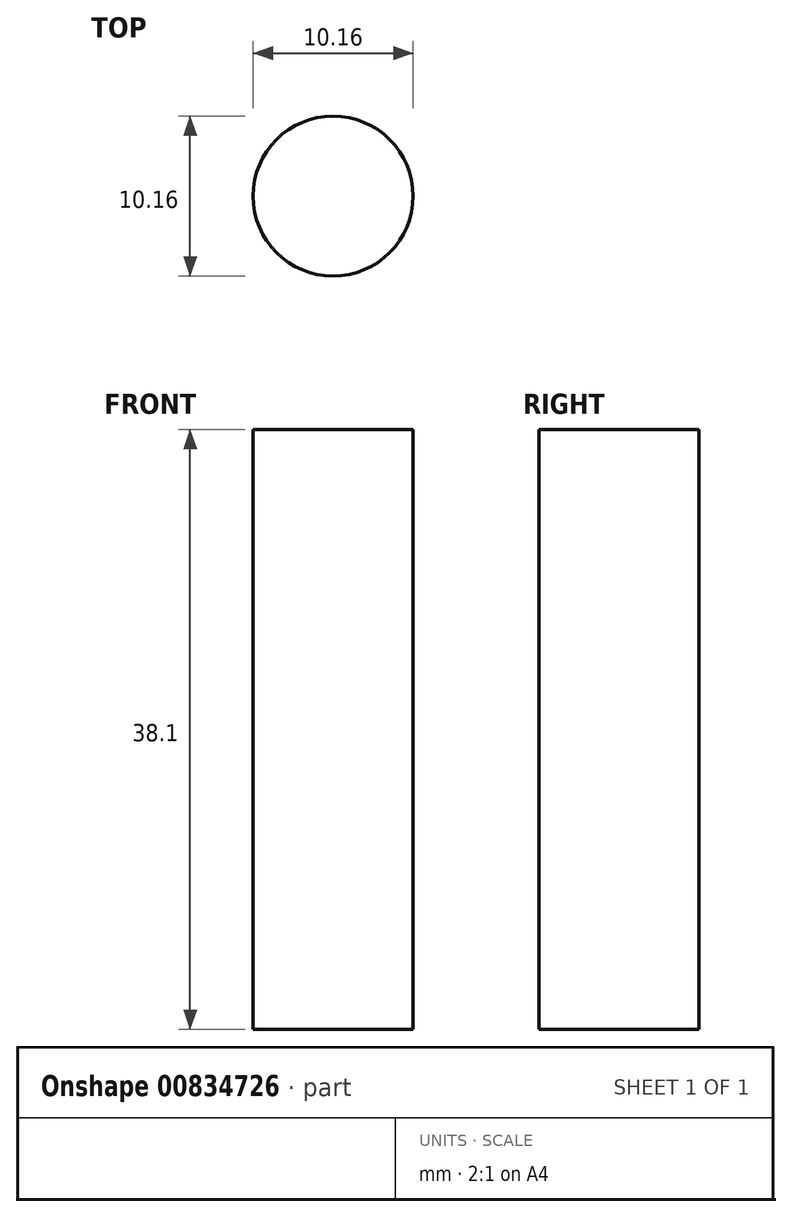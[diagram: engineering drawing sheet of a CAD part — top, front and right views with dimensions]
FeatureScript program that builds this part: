
annotation { "Feature Type Name" : "Feature", "Feature Type Description" : "" }
export const myFeature = defineFeature(function(context is Context, id is Id, definition is map)
    precondition{}
    {
        {
            var Q0;
            Q0=qCreatedBy(makeId("Front.planeOp"),FACE);
            var sketch = newSketch(context, id + "F0", { "sketchPlane" : qUnion([Q0])});
            skLineSegment(sketch, "E0.bottom", {"start": v(-5.9, 16.9) * mm, "end": v(4.26, 16.9) * mm});
            skLineSegment(sketch, "E0.top", {"start": v(-5.9, -21.2) * mm, "end": v(4.26, -21.2) * mm});
            skLineSegment(sketch, "E0.left", {"start": v(-5.9, 16.9) * mm, "end": v(-5.9, -21.2) * mm});
            skLineSegment(sketch, "E0.right", {"start": v(4.26, 16.9) * mm, "end": v(4.26, -21.2) * mm});
            skSolve(sketch);
        }
        {
            var Q0;
            Q0=makeQuery(id+"F0.imprint","IMPRINT",FACE,{"disambiguationData":[TD([[makeQuery(id+"F0.imprint","IMPRINT",EDGE,{"derivedFrom":sQuery(id+"F0.wireOp",EDGE,"E0.bottom")}),-1.0]])]});
            extrude(context, id + "F1", {"entities" : qUnion([Q0]), "depth" : 10.16 * mm, "offsetDistance" : 25.4 * mm});
        }
        {
            var Q0;
            Q0=makeQuery(id+"F1.opExtrude","CAP_EDGE",EDGE,{"disambiguationData":[OSD([sQuery(id+"F0.wireOp",EDGE,"E0.right")])],"isStart":false});
            var Q1;
            Q1=makeQuery(id+"F1.opExtrude","CAP_EDGE",EDGE,{"disambiguationData":[OSD([sQuery(id+"F0.wireOp",EDGE,"E0.left")])],"isStart":false});
            var Q2;
            Q2=makeQuery(id+"F1.opExtrude","CAP_EDGE",EDGE,{"disambiguationData":[OSD([sQuery(id+"F0.wireOp",EDGE,"E0.left")])],"isStart":true});
            var Q3;
            Q3=makeQuery(id+"F1.opExtrude","CAP_EDGE",EDGE,{"disambiguationData":[OSD([sQuery(id+"F0.wireOp",EDGE,"E0.right")])],"isStart":true});
            fillet(context, id + "F2", {"entities" : qUnion([Q0, Q1, Q2, Q3]), "radius" : 5.08 * mm, "tangentPropagation" : true, "allowEdgeOverflow" : false});
        }
    });
